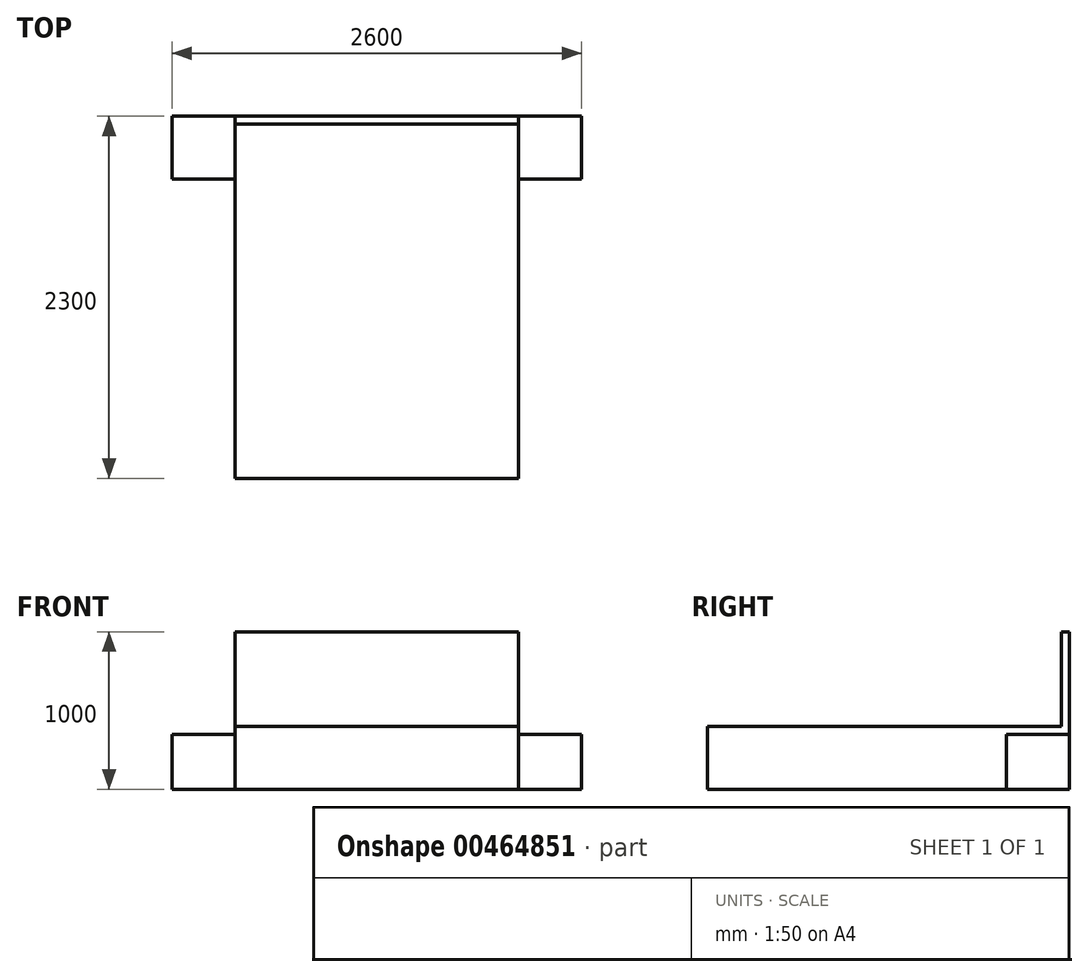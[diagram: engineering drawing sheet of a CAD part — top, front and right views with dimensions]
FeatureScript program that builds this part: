
annotation { "Feature Type Name" : "Feature", "Feature Type Description" : "" }
export const myFeature = defineFeature(function(context is Context, id is Id, definition is map)
    precondition{}
    {
        {
            var Q0;
            Q0=qCreatedBy(makeId("Top.planeOp"),FACE);
            var sketch = newSketch(context, id + "F0", { "sketchPlane" : qUnion([Q0])});
            skLineSegment(sketch, "E0.bottom", {"start": v(-90.96, 0) * mm, "end": v(1709.04, 0) * mm});
            skLineSegment(sketch, "E0.top", {"start": v(-90.96, -2300) * mm, "end": v(1709.04, -2300) * mm});
            skLineSegment(sketch, "E0.left", {"start": v(-90.96, 0) * mm, "end": v(-90.96, -2300) * mm});
            skLineSegment(sketch, "E0.right", {"start": v(1709.04, 0) * mm, "end": v(1709.04, -2300) * mm});
            skSolve(sketch);
        }
        {
            var Q0;
            Q0=makeQuery(id+"F0.imprint","IMPRINT",FACE,{"disambiguationData":[TD([[makeQuery(id+"F0.imprint","IMPRINT",EDGE,{"derivedFrom":sQuery(id+"F0.wireOp",EDGE,"E0.bottom")}),-1.0]])]});
            extrude(context, id + "F1", {"entities" : qUnion([Q0]), "depth" : 400 * mm});
        }
        {
            var Q0;
            Q0=qCreatedBy(makeId("Top.planeOp"),FACE);
            var sketch = newSketch(context, id + "F2", { "sketchPlane" : qUnion([Q0])});
            skLineSegment(sketch, "E1.bottom", {"start": v(1709.04, 0) * mm, "end": v(2109.04, 0) * mm});
            skLineSegment(sketch, "E1.top", {"start": v(1709.04, -400) * mm, "end": v(2109.04, -400) * mm});
            skLineSegment(sketch, "E1.left", {"start": v(1709.04, 0) * mm, "end": v(1709.04, -400) * mm});
            skLineSegment(sketch, "E1.right", {"start": v(2109.04, 0) * mm, "end": v(2109.04, -400) * mm});
            skLineSegment(sketch, "E2", {"start": v(809.04, 533.79) * mm, "end": v(809.04, -935.95) * mm, "construction": true});
            skLineSegment(sketch, "E3.MirrorCS", {"start": v(-490.96, 0) * mm, "end": v(-490.96, -400) * mm});
            skLineSegment(sketch, "E4.MirrorCS", {"start": v(-90.96, 0) * mm, "end": v(-90.96, -400) * mm});
            skLineSegment(sketch, "E5.MirrorCS", {"start": v(-90.96, 0) * mm, "end": v(-490.96, 0) * mm});
            skLineSegment(sketch, "E6.MirrorCS", {"start": v(-90.96, -400) * mm, "end": v(-490.96, -400) * mm});
            skSolve(sketch);
        }
        {
            var Q0;
            Q0 = qSketchRegion(id + "F2", true);
            extrude(context, id + "F3", {"entities" : qUnion([Q0]), "operationType" : NewBodyOperationType.ADD, "depth" : 350 * mm});
        }
        {
            var Q0;
            Q0=makeQuery(id+"F3.boolean.opBoolean","MERGE",FACE,{"derivedFrom":[makeQuery(id+"F1.opExtrude","SWEPT_FACE",FACE,{"disambiguationData":[OSD([sQuery(id+"F0.wireOp",EDGE,"E0.bottom")])]}),makeQuery(id+"F3.opExtrude","SWEPT_FACE",FACE,{"disambiguationData":[OSD([sQuery(id+"F2.wireOp",EDGE,"E1.bottom")])]}),makeQuery(id+"F3.opExtrude","SWEPT_FACE",FACE,{"disambiguationData":[OSD([sQuery(id+"F2.wireOp",EDGE,"E5.MirrorCS")])]})]});
            var sketch = newSketch(context, id + "F4", { "sketchPlane" : qUnion([Q0])});
            skLineSegment(sketch, "E7.bottom", {"start": v(-1709.04, 1000) * mm, "end": v(90.96, 1000) * mm});
            skLineSegment(sketch, "E7.top", {"start": v(-1709.04, 0) * mm, "end": v(90.96, 0) * mm});
            skLineSegment(sketch, "E7.left", {"start": v(-1709.04, 1000) * mm, "end": v(-1709.04, 0) * mm});
            skLineSegment(sketch, "E7.right", {"start": v(90.96, 1000) * mm, "end": v(90.96, 0) * mm});
            skSolve(sketch);
        }
        {
            var Q0;
            Q0 = qSketchRegion(id + "F4", true);
            extrude(context, id + "F5", {"entities" : qUnion([Q0]), "operationType" : NewBodyOperationType.ADD, "oppositeDirection" : true, "depth" : 50 * mm});
        }
    });
